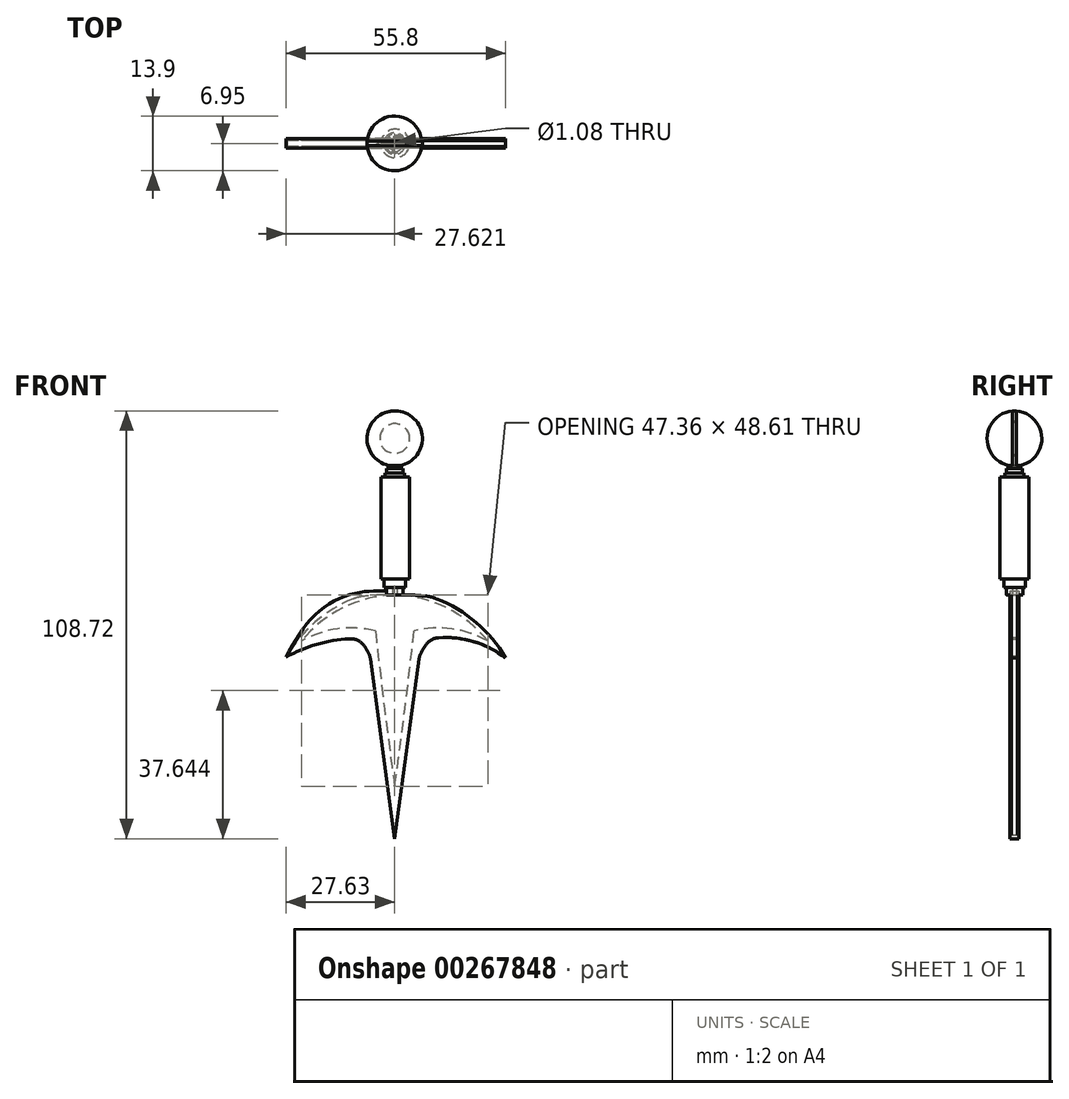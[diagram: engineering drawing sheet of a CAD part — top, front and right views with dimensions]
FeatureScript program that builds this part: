
annotation { "Feature Type Name" : "Feature", "Feature Type Description" : "" }
export const myFeature = defineFeature(function(context is Context, id is Id, definition is map)
    precondition{}
    {
        {
            var Q0;
            Q0=qCreatedBy(makeId("Front.planeOp"),FACE);
            var sketch = newSketch(context, id + "F0", { "sketchPlane" : qUnion([Q0])});
            skCircle(sketch, "E0", {"center": v(0, 53.56) * mm, "radius": 8.26 * mm});
            skCircle(sketch, "E1", {"center": v(0, 53.56) * mm, "radius": 4.45 * mm});
            skLineSegment(sketch, "E2", {"start": v(-4.14, 42.12) * mm, "end": v(-4.14, 11.64) * mm});
            skLineSegment(sketch, "E3", {"start": v(-2.4, 9.1) * mm, "end": v(-2.4, 6.82) * mm});
            skArc(sketch, "E4", {"start": v(-2.4, 6.82) * mm, "mid": v(-5.8, 6.72) * mm, "end": v(-9.19, 6.43) * mm});
            skArc(sketch, "E5", {"start": v(-12.5, 5.59) * mm, "mid": v(-23.95, -1.42) * mm, "end": v(-32.5, -11.77) * mm});
            skArc(sketch, "E6.MirrorCS", {"start": v(1.8, 6.82) * mm, "mid": v(5.48, 6.75) * mm, "end": v(9.16, 6.48) * mm});
            skArc(sketch, "E7.MirrorCS", {"start": v(12.55, 5.66) * mm, "mid": v(24.34, -1.45) * mm, "end": v(33.14, -12.03) * mm});
            skArc(sketch, "E8", {"start": v(-13.54, -6.3) * mm, "mid": v(-23.33, -7.98) * mm, "end": v(-32.5, -11.77) * mm});
            skArc(sketch, "E9", {"start": v(33.14, -12.03) * mm, "mid": v(23.68, -7.17) * mm, "end": v(13.12, -5.97) * mm});
            skArc(sketch, "E10", {"start": v(-7.78, -10.66) * mm, "mid": v(-8.37, -9.58) * mm, "end": v(-9.02, -8.54) * mm});
            skArc(sketch, "E11.MirrorCS", {"start": v(7.78, -10.66) * mm, "mid": v(8.5, -9.36) * mm, "end": v(9.32, -8.1) * mm});
            skLineSegment(sketch, "E12", {"start": v(-7.28, -12.27) * mm, "end": v(0, -66.08) * mm});
            skLineSegment(sketch, "E13.MirrorCS", {"start": v(7.28, -12.27) * mm, "end": v(0, -66.08) * mm});
            skFitSpline(sketch, "E14", {"points": [v(-27.54, -7.23) * mm, v(-12.53, 3.76) * mm, v(0, 6.82) * mm], "startDerivative": vector(23.44, 35.09) * mm, "endDerivative": vector(24.2, 5.64) * mm});
            skArc(sketch, "E15", {"start": v(-5.28, -4.2) * mm, "mid": v(-16.74, -3.28) * mm, "end": v(-27.54, -7.23) * mm});
            skFitSpline(sketch, "E16.MirrorCS", {"points": [v(27.54, -7.23) * mm, v(12.53, 3.76) * mm, v(0, 6.82) * mm], "startDerivative": vector(-23.44, 35.09) * mm, "endDerivative": vector(-24.2, 5.64) * mm});
            skArc(sketch, "E17.MirrorCS", {"start": v(5.97, -4.24) * mm, "mid": v(17.07, -3.46) * mm, "end": v(27.54, -7.23) * mm});
            skLineSegment(sketch, "E18.MirrorCS", {"start": v(2.3, -8.88) * mm, "end": v(0.14, -53.88) * mm, "construction": true});
            skPoint(sketch, "E19.visualSharp", {"position": v(-10.83, -6.22) * mm});
            skArc(sketch, "E19.filletArc", {"start": v(-9.02, -8.54) * mm, "mid": v(-10.98, -6.82) * mm, "end": v(-13.54, -6.3) * mm});
            skPoint(sketch, "E20.visualSharp", {"position": v(-7.39, -11.49) * mm});
            skArc(sketch, "E20.filletArc", {"start": v(-7.28, -12.27) * mm, "mid": v(-7.46, -11.44) * mm, "end": v(-7.78, -10.66) * mm});
            skPoint(sketch, "E21.visualSharp", {"position": v(7.39, -11.49) * mm});
            skArc(sketch, "E21.filletArc", {"start": v(7.78, -10.66) * mm, "mid": v(7.46, -11.44) * mm, "end": v(7.28, -12.27) * mm});
            skPoint(sketch, "E22.visualSharp", {"position": v(10.83, -6.22) * mm});
            skArc(sketch, "E22.filletArc", {"start": v(13.12, -5.97) * mm, "mid": v(10.98, -6.61) * mm, "end": v(9.32, -8.1) * mm});
            skPoint(sketch, "E23.visualSharp", {"position": v(-10.83, 6.22) * mm});
            skArc(sketch, "E23.filletArc", {"start": v(-9.19, 6.43) * mm, "mid": v(-10.87, 6.12) * mm, "end": v(-12.5, 5.59) * mm});
            skPoint(sketch, "E24.visualSharp", {"position": v(10.83, 6.3) * mm});
            skArc(sketch, "E24.filletArc", {"start": v(12.55, 5.66) * mm, "mid": v(10.88, 6.19) * mm, "end": v(9.16, 6.48) * mm});
            skArc(sketch, "E25.filletArc", {"start": v(4.83, 5.77) * mm, "mid": v(0, 6.28) * mm, "end": v(-4.83, 5.77) * mm});
            skPoint(sketch, "E26.visualSharp", {"position": v(-2.4, -5.26) * mm});
            skPoint(sketch, "E27.visualSharp", {"position": v(2.45, -5.52) * mm});
            skArc(sketch, "E27.filletArc", {"start": v(5.97, -4.24) * mm, "mid": v(3.39, -5.97) * mm, "end": v(2.3, -8.88) * mm});
            skPoint(sketch, "E28.visualSharp", {"position": v(3, 44.66) * mm});
            skLineSegment(sketch, "E29", {"start": v(-2.84, 43.24) * mm, "end": v(-2.84, 42.12) * mm});
            skLineSegment(sketch, "E30", {"start": v(0.67, 76.5) * mm, "end": v(0, -91.66) * mm, "construction": true});
            skLineSegment(sketch, "E31", {"start": v(0.02, 44.66) * mm, "end": v(0.01, 43.24) * mm});
            skLineSegment(sketch, "E32", {"start": v(-2.4, 44.66) * mm, "end": v(-2.4, 43.24) * mm});
            skLineSegment(sketch, "E33", {"start": v(-0.08, 45.31) * mm, "end": v(-0.08, 44.66) * mm});
            skPoint(sketch, "E33.startSnap0", {"position": v(-0.08, 44.66) * mm});
            skLineSegment(sketch, "E34", {"start": v(1.85, 45.52) * mm, "end": v(1.85, 44.66) * mm});
            skLineSegment(sketch, "E35", {"start": v(0.02, 44.66) * mm, "end": v(-2.4, 44.66) * mm});
            skLineSegment(sketch, "E36", {"start": v(1.85, 44.66) * mm, "end": v(-0.08, 44.66) * mm});
            skLineSegment(sketch, "E37", {"start": v(0.02, 43.24) * mm, "end": v(0.02, 42.12) * mm});
            skLineSegment(sketch, "E38", {"start": v(-2.84, 43.24) * mm, "end": v(0.02, 43.24) * mm});
            skLineSegment(sketch, "E39", {"start": v(-3.23, 9.1) * mm, "end": v(-3.23, 11.64) * mm});
            skLineSegment(sketch, "E40", {"start": v(0, 9.1) * mm, "end": v(0, 11.64) * mm});
            skLineSegment(sketch, "E41", {"start": v(-3.23, 9.1) * mm, "end": v(0, 9.1) * mm});
            skLineSegment(sketch, "E42", {"start": v(-2.4, 6.82) * mm, "end": v(1.8, 6.82) * mm});
            skLineSegment(sketch, "E43", {"start": v(-0.01, 6.82) * mm, "end": v(-0.01, 9.1) * mm});
            skLineSegment(sketch, "E44", {"start": v(-0.01, 9.1) * mm, "end": v(-2.4, 9.1) * mm});
            skLineSegment(sketch, "E45", {"start": v(0.14, 42.12) * mm, "end": v(0.14, 11.64) * mm});
            skLineSegment(sketch, "E46", {"start": v(-4.14, 11.64) * mm, "end": v(0.14, 11.64) * mm});
            skLineSegment(sketch, "E47", {"start": v(-2.84, 42.12) * mm, "end": v(0.02, 42.12) * mm});
            skLineSegment(sketch, "E48", {"start": v(-4.14, 42.12) * mm, "end": v(0.14, 42.12) * mm});
            skLineSegment(sketch, "E49", {"start": v(-3.23, 11.64) * mm, "end": v(0, 11.64) * mm});
            skFitSpline(sketch, "E50", {"points": [v(-2.4, 7.96) * mm, v(-10.83, 7.52) * mm, v(-22.65, 1.92) * mm, v(-32.5, -11.77) * mm], "startDerivative": vector(-29.32, -0.31) * mm, "endDerivative": vector(-22.24, -40.9) * mm});
            skPoint(sketch, "E51.1.internal.snap0", {"position": v(0, 10.37) * mm});
            skFitSpline(sketch, "E51", {"points": [v(-2.4, 7.96) * mm, v(0, 7.96) * mm], "startDerivative": vector(2.4, 0) * mm, "endDerivative": vector(2.4, 0) * mm});
            skFitSpline(sketch, "E52.MirrorCS", {"points": [v(3.18, 7.94) * mm, v(11.62, 7.43) * mm, v(23.39, 1.74) * mm, v(33.14, -12.03) * mm], "startDerivative": vector(29.32, -0.54) * mm, "endDerivative": vector(21.92, -41.07) * mm});
            skFitSpline(sketch, "E53.MirrorCS", {"points": [v(3.18, 7.94) * mm, v(0.79, 7.96) * mm], "startDerivative": vector(-2.4, 0.02) * mm, "endDerivative": vector(-2.4, 0.02) * mm});
            skLineSegment(sketch, "E54", {"start": v(3.18, 6.81) * mm, "end": v(3.18, 7.94) * mm});
            skLineSegment(sketch, "E55.MirrorCS", {"start": v(-1.64, -8.87) * mm, "end": v(0.16, -53.88) * mm, "construction": true});
            skArc(sketch, "E56.MirrorCS", {"start": v(-5.28, -4.2) * mm, "mid": v(-2.7, -5.95) * mm, "end": v(-1.64, -8.87) * mm});
            skSolve(sketch);
        }
        {
            var Q0;
            Q0=makeQuery(id+"F0.imprint","IMPRINT",FACE,{"disambiguationData":[TD([[makeQuery(id+"F0.imprint","IMPRINT",EDGE,{"derivedFrom":sQuery(id+"F0.wireOp",EDGE,"E1")}),-1.0]])]});
            extrude(context, id + "F1", {"entities" : qUnion([Q0]), "endBound" : BoundingType.SYMMETRIC, "depth" : 1.27 * mm});
        }
        {
            var Q0;
            {var subQ3=sQuery(id+"F0.wireOp",EDGE,"E3");Q0=makeQuery(id+"F0.imprint","IMPRINT",FACE,{"disambiguationData":[TD([[makeQuery(id+"F0.imprint","IMPRINT",EDGE,{"derivedFrom":subQ3}),1.0]])]});}
            extrude(context, id + "F2", {"entities" : qUnion([Q0]), "operationType" : NewBodyOperationType.ADD, "endBound" : BoundingType.SYMMETRIC, "depth" : 1.27 * mm});
        }
        {
            var Q0;
            {var subQ0=sQuery(id+"F0.wireOp",EDGE,"E4");Q0=makeQuery(id+"F0.imprint","IMPRINT",FACE,{"disambiguationData":[TD([[makeQuery(id+"F0.imprint","IMPRINT",EDGE,{"derivedFrom":subQ0}),1.0]])]});}
            var Q1;
            Q1=makeQuery(id+"F0.imprint","IMPRINT",FACE,{"disambiguationData":[TD([[makeQuery(id+"F0.imprint","IMPRINT",EDGE,{"derivedFrom":sQuery(id+"F0.wireOp",EDGE,"E14")}),-1.0]])]});
            extrude(context, id + "F3", {"entities" : qUnion([Q0, Q1]), "operationType" : NewBodyOperationType.ADD, "endBound" : BoundingType.SYMMETRIC, "depth" : 1.78 * mm});
        }
        {
            var Q0;
            Q0=qCreatedBy(makeId("Front.planeOp"),FACE);
            var sketch = newSketch(context, id + "F4", { "sketchPlane" : qUnion([Q0])});
            skArc(sketch, "E57", {"start": v(27.86, -6.98) * mm, "mid": v(15.44, 2.96) * mm, "end": v(0, 6.8) * mm});
            skArc(sketch, "E58", {"start": v(27.86, -6.98) * mm, "mid": v(17.1, -3.34) * mm, "end": v(5.75, -4) * mm});
            skArc(sketch, "E59", {"start": v(0, -50.39) * mm, "mid": v(3.07, -27.21) * mm, "end": v(5.75, -4) * mm});
            skArc(sketch, "E60.MirrorCS", {"start": v(0, -50.39) * mm, "mid": v(-3.07, -27.21) * mm, "end": v(-5.75, -4) * mm});
            skArc(sketch, "E61.MirrorCS", {"start": v(-27.86, -6.98) * mm, "mid": v(-17.1, -3.34) * mm, "end": v(-5.75, -4) * mm});
            skArc(sketch, "E62.MirrorCS", {"start": v(-27.86, -6.98) * mm, "mid": v(-15.44, 2.96) * mm, "end": v(0, 6.8) * mm});
            skSolve(sketch);
        }
        {
            var Q0;
            Q0 = qSketchRegion(id + "F4", true);
            extrude(context, id + "F5", {"entities" : qUnion([Q0]), "operationType" : NewBodyOperationType.ADD, "endBound" : BoundingType.SYMMETRIC, "depth" : 2.54 * mm});
        }
        {
            var Q0;
            {var subQ0=sQuery(id+"F0.wireOp",EDGE,"E31");Q0=makeQuery(id+"F0.imprint","IMPRINT",FACE,{"disambiguationData":[TD([[makeQuery(id+"F0.imprint","IMPRINT",EDGE,{"derivedFrom":subQ0}),-1.0]])]});}
            var Q1;
            Q1=sQuery(id+"F0.wireOp",EDGE,"E31");
            revolve(context, id + "F6", {"operationType" : NewBodyOperationType.ADD, "entities" : qUnion([Q0]), "axis" : qUnion([Q1]), "revolveType" : RevolveType.FULL});
        }
        {
            var Q0;
            {var subQ1=sQuery(id+"F0.wireOp",EDGE,"E33");Q0=makeQuery(id+"F0.imprint","IMPRINT",FACE,{"disambiguationData":[TD([[makeQuery(id+"F0.imprint","IMPRINT",EDGE,{"derivedFrom":subQ1}),1.0]])]});}
            var Q1;
            Q1=sQuery(id+"F0.wireOp",EDGE,"E33");
            revolve(context, id + "F7", {"entities" : qUnion([Q0]), "axis" : qUnion([Q1]), "revolveType" : RevolveType.FULL});
        }
        {
            var Q0;
            {var subQ2=sQuery(id+"F0.wireOp",EDGE,"E29");Q0=makeQuery(id+"F0.imprint","IMPRINT",FACE,{"disambiguationData":[TD([[makeQuery(id+"F0.imprint","IMPRINT",EDGE,{"derivedFrom":subQ2}),1.0]])]});}
            var Q1;
            Q1=sQuery(id+"F0.wireOp",EDGE,"E37");
            revolve(context, id + "F8", {"entities" : qUnion([Q0]), "axis" : qUnion([Q1]), "revolveType" : RevolveType.FULL});
        }
        {
            var Q0;
            {var subQ2=sQuery(id+"F0.wireOp",EDGE,"E39");Q0=makeQuery(id+"F0.imprint","IMPRINT",FACE,{"disambiguationData":[TD([[makeQuery(id+"F0.imprint","IMPRINT",EDGE,{"derivedFrom":subQ2}),-1.0]])]});}
            var Q1;
            Q1=sQuery(id+"F0.wireOp",EDGE,"E40");
            revolve(context, id + "F9", {"entities" : qUnion([Q0]), "axis" : qUnion([Q1]), "revolveType" : RevolveType.FULL});
        }
        {
            var Q0;
            Q0=makeQuery(id+"F2.opExtrude","CAP_FACE",FACE,{"disambiguationData":[OSD([sQuery(id+"F0.wireOp",EDGE,"E3"),sQuery(id+"F0.wireOp",EDGE,"E42"),sQuery(id+"F0.wireOp",EDGE,"E43"),sQuery(id+"F0.wireOp",EDGE,"E44")])],"isStart":false});
            var Q1;
            Q1=sQuery(id+"F0.wireOp",EDGE,"E43");
            revolve(context, id + "F10", {"entities" : qUnion([Q0]), "axis" : qUnion([Q1]), "revolveType" : RevolveType.FULL});
        }
        {
            var Q0;
            Q0=makeQuery(id+"F1.opExtrude","CAP_EDGE",EDGE,{"disambiguationData":[OSD([sQuery(id+"F0.wireOp",EDGE,"E1")])],"isStart":false});
            fillet(context, id + "F11", {"entities" : qUnion([Q0]), "radius" : 2.54 * mm, "tangentPropagation" : true, "allowEdgeOverflow" : false});
        }
        {
            var Q0;
            Q0=makeQuery(id+"F3.opExtrude","SWEPT_EDGE",EDGE,{"disambiguationData":[OSD([sQuery(id+"F0.wireOp",EDGE,"E5"),sQuery(id+"F0.wireOp",EDGE,"E8")])]});
            var Q1;
            Q1=makeQuery(id+"F3.opExtrude","SWEPT_EDGE",EDGE,{"disambiguationData":[OSD([sQuery(id+"F0.wireOp",EDGE,"E7.MirrorCS"),sQuery(id+"F0.wireOp",EDGE,"E9")])]});
            var Q2;
            Q2=makeQuery(id+"F3.opExtrude","SWEPT_EDGE",EDGE,{"disambiguationData":[OSD([sQuery(id+"F0.wireOp",EDGE,"E12"),sQuery(id+"F0.wireOp",EDGE,"E13.MirrorCS")])]});
            fillet(context, id + "F12", {"entities" : qUnion([Q0, Q1, Q2]), "radius" : 0.15 * mm, "tangentPropagation" : true, "allowEdgeOverflow" : false});
        }
        {
            var Q0;
            {var subQ3=sQuery(id+"F0.wireOp",EDGE,"E2");Q0=makeQuery(id+"F0.imprint","IMPRINT",FACE,{"disambiguationData":[TD([[makeQuery(id+"F0.imprint","IMPRINT",EDGE,{"derivedFrom":subQ3}),1.0]])]});}
            var Q1;
            Q1=sQuery(id+"F0.wireOp",EDGE,"E45");
            revolve(context, id + "F13", {"entities" : qUnion([Q0]), "axis" : qUnion([Q1]), "revolveType" : RevolveType.FULL});
        }
        {
            var Q0;
            {var subQ0=sQuery(id+"F0.wireOp",EDGE,"E4");Q0=makeQuery(id+"F0.imprint","IMPRINT",FACE,{"disambiguationData":[TD([[makeQuery(id+"F0.imprint","IMPRINT",EDGE,{"derivedFrom":subQ0}),-1.0]])]});}
            var Q1;
            Q1=makeQuery(id+"F0.imprint","IMPRINT",FACE,{"disambiguationData":[TD([[makeQuery(id+"F0.imprint","IMPRINT",EDGE,{"derivedFrom":sQuery(id+"F0.wireOp",EDGE,"E7.MirrorCS")}),1.0]])]});
            extrude(context, id + "F14", {"entities" : qUnion([Q0, Q1]), "endBound" : BoundingType.SYMMETRIC, "depth" : 2.8 * mm});
        }
        {
            var Q0;
            Q0=makeQuery(id+"F1.opExtrude","SWEPT_BODY",BODY,{"disambiguationData":[OSD([sQuery(id+"F0.wireOp",EDGE,"E0"),sQuery(id+"F0.wireOp",EDGE,"E1")])]});
            var Q1;
            Q1=makeQuery(id+"F2.opExtrude","SWEPT_BODY",BODY,{"disambiguationData":[OSD([sQuery(id+"F0.wireOp",EDGE,"E3"),sQuery(id+"F0.wireOp",EDGE,"E42"),sQuery(id+"F0.wireOp",EDGE,"E43"),sQuery(id+"F0.wireOp",EDGE,"E44")])]});
            var Q2;
            Q2=makeQuery(id+"F3.opExtrude","SWEPT_BODY",BODY,{"disambiguationData":[OSD([sQuery(id+"F0.wireOp",EDGE,"E4"),sQuery(id+"F0.wireOp",EDGE,"E5"),sQuery(id+"F0.wireOp",EDGE,"E6.MirrorCS"),sQuery(id+"F0.wireOp",EDGE,"E7.MirrorCS"),sQuery(id+"F0.wireOp",EDGE,"E8"),sQuery(id+"F0.wireOp",EDGE,"E9"),sQuery(id+"F0.wireOp",EDGE,"E10"),sQuery(id+"F0.wireOp",EDGE,"E11.MirrorCS"),sQuery(id+"F0.wireOp",EDGE,"E12"),sQuery(id+"F0.wireOp",EDGE,"E13.MirrorCS"),sQuery(id+"F0.wireOp",EDGE,"E19.filletArc"),sQuery(id+"F0.wireOp",EDGE,"E20.filletArc"),sQuery(id+"F0.wireOp",EDGE,"E21.filletArc"),sQuery(id+"F0.wireOp",EDGE,"E22.filletArc"),sQuery(id+"F0.wireOp",EDGE,"E23.filletArc"),sQuery(id+"F0.wireOp",EDGE,"E24.filletArc"),sQuery(id+"F0.wireOp",EDGE,"E42")])]});
            var Q3;
            Q3=makeQuery(id+"F5.opExtrude","SWEPT_BODY",BODY,{"disambiguationData":[OSD([sQuery(id+"F4.wireOp",EDGE,"E57"),sQuery(id+"F4.wireOp",EDGE,"E58"),sQuery(id+"F4.wireOp",EDGE,"E59"),sQuery(id+"F4.wireOp",EDGE,"E60.MirrorCS"),sQuery(id+"F4.wireOp",EDGE,"E61.MirrorCS"),sQuery(id+"F4.wireOp",EDGE,"E62.MirrorCS")])]});
            var Q4;
            Q4=makeQuery(id+"F6.opRevolve","SWEPT_BODY",BODY,{"disambiguationData":[OSD([sQuery(id+"F0.wireOp",EDGE,"E31"),sQuery(id+"F0.wireOp",EDGE,"E32"),sQuery(id+"F0.wireOp",EDGE,"E35"),sQuery(id+"F0.wireOp",EDGE,"E36"),sQuery(id+"F0.wireOp",EDGE,"E38")])]});
            var Q5;
            Q5=makeQuery(id+"F7.opRevolve","SWEPT_BODY",BODY,{"disambiguationData":[OSD([sQuery(id+"F0.wireOp",EDGE,"E0"),sQuery(id+"F0.wireOp",EDGE,"E33"),sQuery(id+"F0.wireOp",EDGE,"E34"),sQuery(id+"F0.wireOp",EDGE,"E36")])]});
            var Q6;
            Q6=makeQuery(id+"F8.opRevolve","SWEPT_BODY",BODY,{"disambiguationData":[OSD([sQuery(id+"F0.wireOp",EDGE,"E29"),sQuery(id+"F0.wireOp",EDGE,"E37"),sQuery(id+"F0.wireOp",EDGE,"E38"),sQuery(id+"F0.wireOp",EDGE,"E48")])]});
            var Q7;
            Q7=makeQuery(id+"F9.opRevolve","SWEPT_BODY",BODY,{"disambiguationData":[OSD([sQuery(id+"F0.wireOp",EDGE,"E39"),sQuery(id+"F0.wireOp",EDGE,"E40"),sQuery(id+"F0.wireOp",EDGE,"E41"),sQuery(id+"F0.wireOp",EDGE,"E44"),sQuery(id+"F0.wireOp",EDGE,"E49")])]});
            var Q8;
            Q8=makeQuery(id+"F10.opRevolve","SWEPT_BODY",BODY,{"disambiguationData":[OSD([sQuery(id+"F0.wireOp",EDGE,"E3"),sQuery(id+"F0.wireOp",EDGE,"E42"),sQuery(id+"F0.wireOp",EDGE,"E43"),sQuery(id+"F0.wireOp",EDGE,"E44")])]});
            var Q9;
            Q9=makeQuery(id+"F13.opRevolve","SWEPT_BODY",BODY,{"disambiguationData":[OSD([sQuery(id+"F0.wireOp",EDGE,"E2"),sQuery(id+"F0.wireOp",EDGE,"E45"),sQuery(id+"F0.wireOp",EDGE,"E46"),sQuery(id+"F0.wireOp",EDGE,"E48"),sQuery(id+"F0.wireOp",EDGE,"E49")])]});
            var Q10;
            Q10=makeQuery(id+"F14.opExtrude","SWEPT_BODY",BODY,{"disambiguationData":[OSD([sQuery(id+"F0.wireOp",EDGE,"E3"),sQuery(id+"F0.wireOp",EDGE,"E4"),sQuery(id+"F0.wireOp",EDGE,"E5"),sQuery(id+"F0.wireOp",EDGE,"E23.filletArc"),sQuery(id+"F0.wireOp",EDGE,"E50")])]});
            var Q11;
            Q11=makeQuery(id+"F14.opExtrude","SWEPT_BODY",BODY,{"disambiguationData":[OSD([sQuery(id+"F0.wireOp",EDGE,"E6.MirrorCS"),sQuery(id+"F0.wireOp",EDGE,"E7.MirrorCS"),sQuery(id+"F0.wireOp",EDGE,"E24.filletArc"),sQuery(id+"F0.wireOp",EDGE,"E52.MirrorCS"),sQuery(id+"F0.wireOp",EDGE,"E54")])]});
            var Q12;
            Q12=qCreatedBy(makeId("Origin.pointOp"),VERTEX);
            var Q13;
            Q13=qCreatedBy(makeId("Origin.pointOp"),VERTEX);
            transform(context, id + "F15", {"entities" : qUnion([Q0, Q1, Q2, Q3, Q4, Q5, Q6, Q7, Q8, Q9, Q10, Q11]), "transformType" : TransformType.SCALE_UNIFORMLY, "scale" : .85, "scalePoint" : qUnion([Q13]), "makeCopy" : false});
        }
    });
